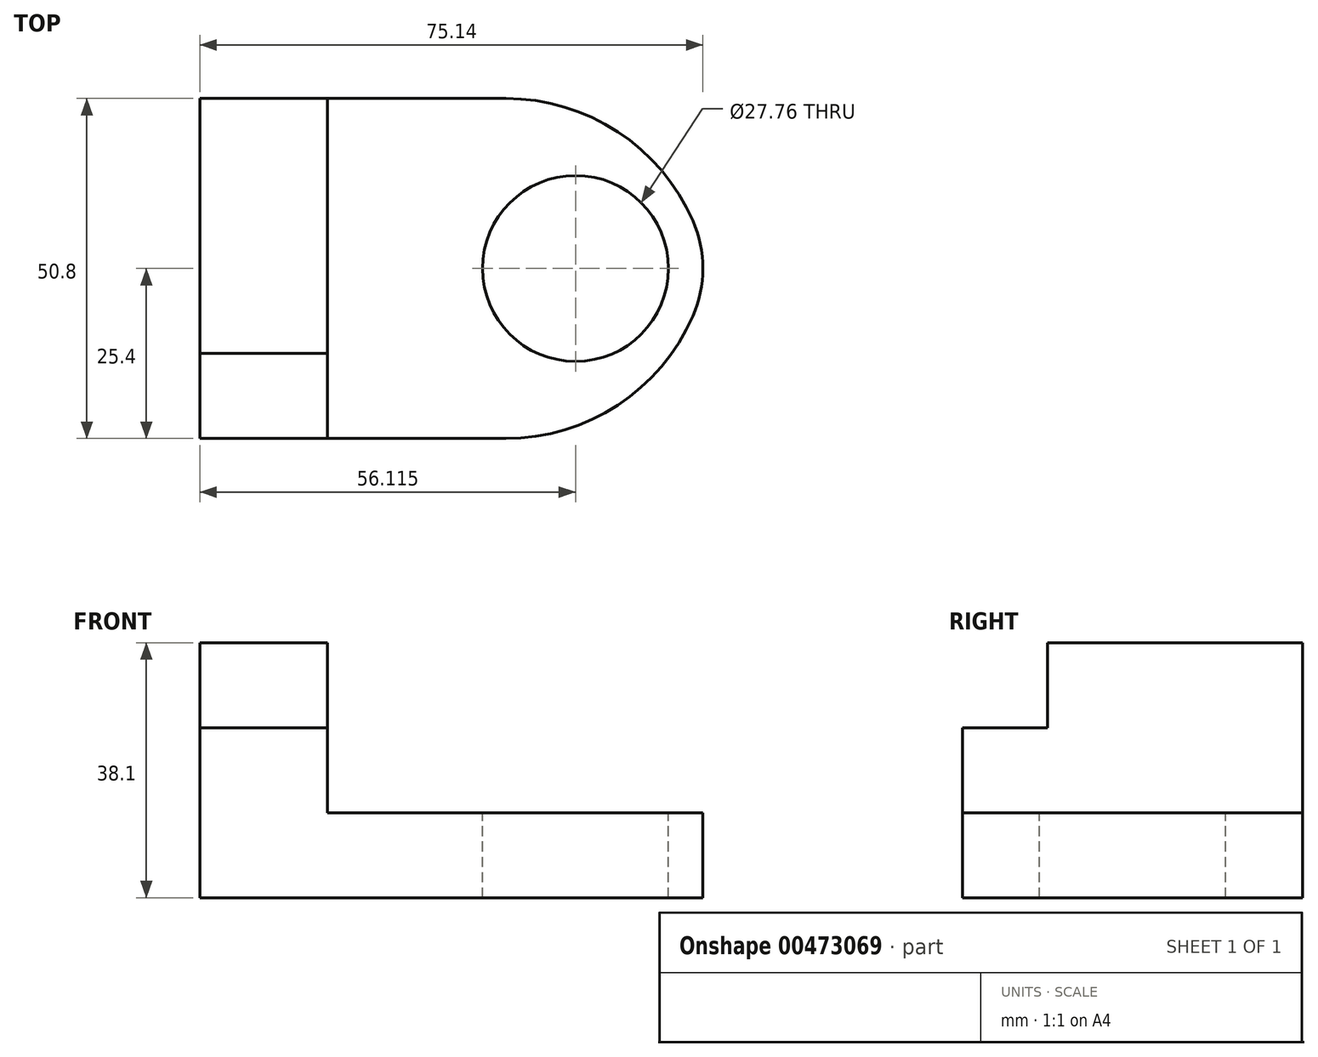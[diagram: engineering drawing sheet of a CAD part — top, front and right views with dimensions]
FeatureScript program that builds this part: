
annotation { "Feature Type Name" : "Feature", "Feature Type Description" : "" }
export const myFeature = defineFeature(function(context is Context, id is Id, definition is map)
    precondition{}
    {
        {
            var Q0;
            Q0=qCreatedBy(makeId("Top.planeOp"),FACE);
            var sketch = newSketch(context, id + "F0", { "sketchPlane" : qUnion([Q0])});
            skLineSegment(sketch, "E0.bottom", {"start": v(7.62, 25.4) * mm, "end": v(-38.1, 25.4) * mm});
            skLineSegment(sketch, "E0.top", {"start": v(7.62, -25.4) * mm, "end": v(-38.1, -25.4) * mm});
            skLineSegment(sketch, "E0.left", {"start": v(38.1, 5.08) * mm, "end": v(38.1, -5.08) * mm});
            skLineSegment(sketch, "E0.right", {"start": v(-38.1, 25.4) * mm, "end": v(-38.1, -25.4) * mm});
            skPoint(sketch, "E0.middle", {"position": v(0, 0) * mm});
            skPoint(sketch, "E1.visualSharp", {"position": v(38.1, 25.4) * mm});
            skArc(sketch, "E1.filletArc", {"start": v(38.1, -5.08) * mm, "mid": v(29.17, 16.47) * mm, "end": v(7.62, 25.4) * mm});
            skPoint(sketch, "E2.visualSharp", {"position": v(38.1, -25.4) * mm});
            skArc(sketch, "E2.filletArc", {"start": v(7.62, -25.4) * mm, "mid": v(29.17, -16.47) * mm, "end": v(38.1, 5.08) * mm});
            skSolve(sketch);
        }
        {
            var Q0;
            {var subQ2=sQuery(id+"F0.wireOp",EDGE,"E0.bottom");Q0=makeQuery(id+"F0.imprint","IMPRINT",FACE,{"disambiguationData":[TD([[makeQuery(id+"F0.imprint","IMPRINT",EDGE,{"derivedFrom":subQ2}),1.0]])]});}
            extrude(context, id + "F1", {"entities" : qUnion([Q0]), "depth" : 12.7 * mm});
        }
        {
            var Q0;
            Q0=makeQuery(id+"F1.opExtrude","CAP_FACE",FACE,{"disambiguationData":[OSD([sQuery(id+"F0.wireOp",EDGE,"E0.bottom"),sQuery(id+"F0.wireOp",EDGE,"E0.top"),sQuery(id+"F0.wireOp",EDGE,"E0.right"),sQuery(id+"F0.wireOp",EDGE,"E1.filletArc"),sQuery(id+"F0.wireOp",EDGE,"E2.filletArc")])],"isStart":false});
            var sketch = newSketch(context, id + "F2", { "sketchPlane" : qUnion([Q0])});
            skLineSegment(sketch, "E3.bottom", {"start": v(-38.1, -25.4) * mm, "end": v(-19.05, -25.4) * mm});
            skLineSegment(sketch, "E3.top", {"start": v(-38.1, 25.4) * mm, "end": v(-19.05, 25.4) * mm});
            skLineSegment(sketch, "E3.left", {"start": v(-38.1, -25.4) * mm, "end": v(-38.1, 25.4) * mm});
            skLineSegment(sketch, "E3.right", {"start": v(-19.05, -25.4) * mm, "end": v(-19.05, 25.4) * mm});
            skSolve(sketch);
        }
        {
            var Q0;
            Q0=makeQuery(id+"F2.imprint","IMPRINT",FACE,{"disambiguationData":[TD([[makeQuery(id+"F2.imprint","IMPRINT",EDGE,{"derivedFrom":sQuery(id+"F2.wireOp",EDGE,"E3.bottom")}),-1.0]])]});
            extrude(context, id + "F3", {"entities" : qUnion([Q0]), "operationType" : NewBodyOperationType.ADD, "depth" : 25.4 * mm});
        }
        {
            var Q0;
            Q0=makeQuery(id+"F3.opExtrude","CAP_FACE",FACE,{"disambiguationData":[OSD([sQuery(id+"F2.wireOp",EDGE,"E3.bottom"),sQuery(id+"F2.wireOp",EDGE,"E3.top"),sQuery(id+"F2.wireOp",EDGE,"E3.left"),sQuery(id+"F2.wireOp",EDGE,"E3.right")])],"isStart":false});
            var sketch = newSketch(context, id + "F4", { "sketchPlane" : qUnion([Q0])});
            skLineSegment(sketch, "E4.bottom", {"start": v(-38.1, -25.4) * mm, "end": v(-19.05, -25.4) * mm});
            skLineSegment(sketch, "E4.top", {"start": v(-38.1, -12.7) * mm, "end": v(-19.05, -12.7) * mm});
            skLineSegment(sketch, "E4.left", {"start": v(-38.1, -25.4) * mm, "end": v(-38.1, -12.7) * mm});
            skLineSegment(sketch, "E4.right", {"start": v(-19.05, -25.4) * mm, "end": v(-19.05, -12.7) * mm});
            skSolve(sketch);
        }
        {
            var Q0;
            Q0=makeQuery(id+"F4.imprint","IMPRINT",FACE,{"disambiguationData":[TD([[makeQuery(id+"F4.imprint","IMPRINT",EDGE,{"derivedFrom":sQuery(id+"F4.wireOp",EDGE,"E4.bottom")}),-1.0]])]});
            extrude(context, id + "F5", {"entities" : qUnion([Q0]), "operationType" : NewBodyOperationType.REMOVE, "oppositeDirection" : true, "depth" : 12.7 * mm});
        }
        {
            var Q0;
            Q0=makeQuery(id+"F1.opExtrude","CAP_FACE",FACE,{"disambiguationData":[OSD([sQuery(id+"F0.wireOp",EDGE,"E0.bottom"),sQuery(id+"F0.wireOp",EDGE,"E0.top"),sQuery(id+"F0.wireOp",EDGE,"E0.right"),sQuery(id+"F0.wireOp",EDGE,"E1.filletArc"),sQuery(id+"F0.wireOp",EDGE,"E2.filletArc")])],"isStart":false});
            var sketch = newSketch(context, id + "F6", { "sketchPlane" : qUnion([Q0])});
            skCircle(sketch, "E5", {"center": v(18.02, 0) * mm, "radius": 13.88 * mm});
            skSolve(sketch);
        }
        {
            var Q0;
            Q0=makeQuery(id+"F6.imprint","IMPRINT",FACE,{"disambiguationData":[TD([[makeQuery(id+"F6.imprint","IMPRINT",EDGE,{"derivedFrom":sQuery(id+"F6.wireOp",EDGE,"E5")}),1.0]])]});
            extrude(context, id + "F7", {"entities" : qUnion([Q0]), "operationType" : NewBodyOperationType.REMOVE, "oppositeDirection" : true, "depth" : 12.7 * mm});
        }
        {
            var Q0;
            Q0=makeQuery(id+"F1.opExtrude","SWEPT_EDGE",EDGE,{"disambiguationData":[OSD([sQuery(id+"F0.wireOp",EDGE,"E1.filletArc"),sQuery(id+"F0.wireOp",EDGE,"E2.filletArc")])]});
            fillet(context, id + "F8", {"entities" : qUnion([Q0]), "radius" : 17.78 * mm, "tangentPropagation" : true, "allowEdgeOverflow" : false});
        }
    });
